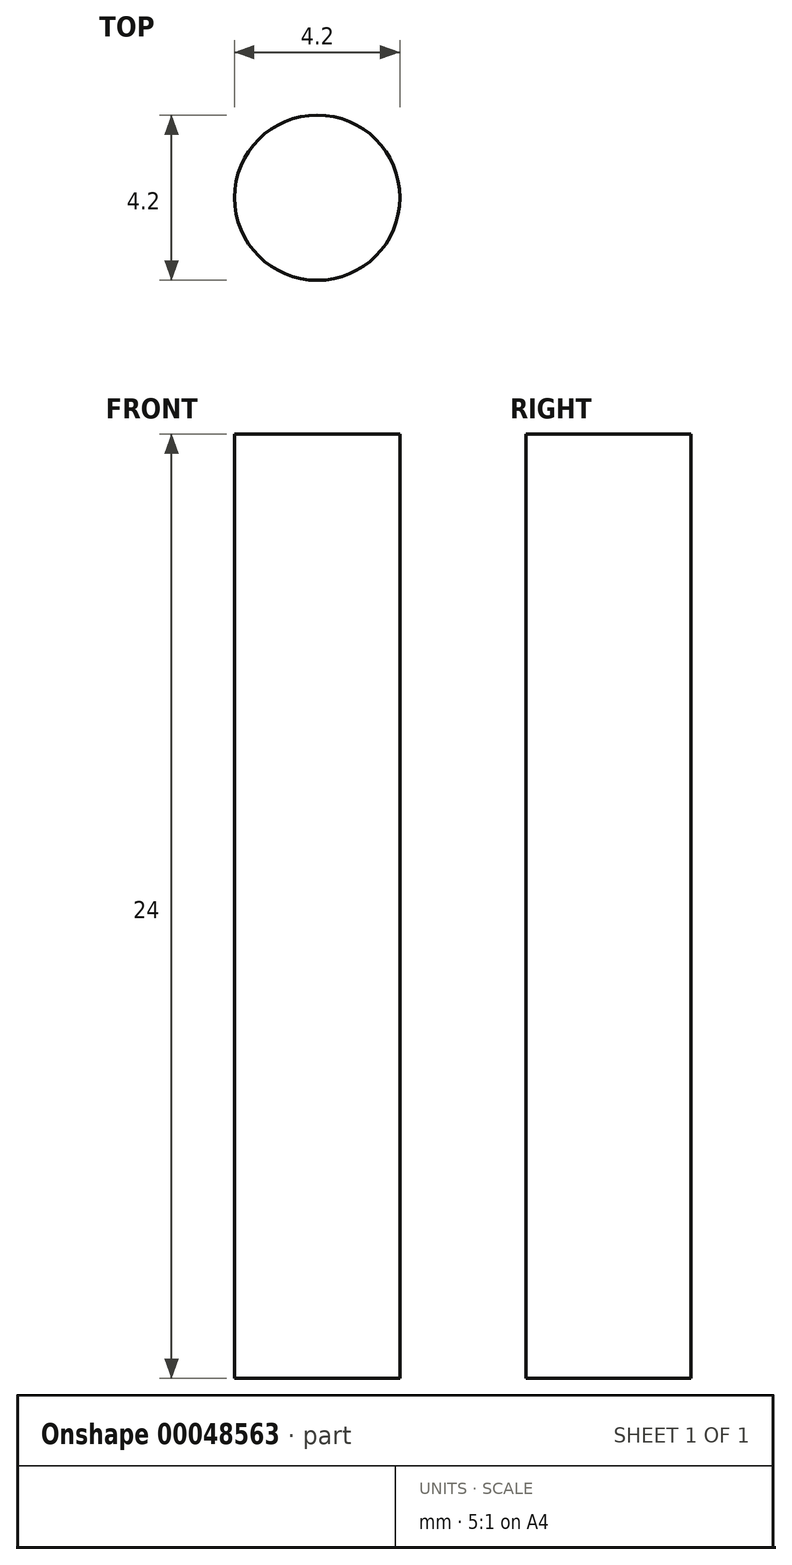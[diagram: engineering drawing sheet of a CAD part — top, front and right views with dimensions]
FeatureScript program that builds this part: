
annotation { "Feature Type Name" : "Feature", "Feature Type Description" : "" }
export const myFeature = defineFeature(function(context is Context, id is Id, definition is map)
    precondition{}
    {
        {
            var Q0;
            Q0=qCreatedBy(makeId("Top.planeOp"),FACE);
            var sketch = newSketch(context, id + "F0", { "sketchPlane" : qUnion([Q0])});
            skCircle(sketch, "E0", {"center": v(0, 0) * mm, "radius": 2.1 * mm});
            skSolve(sketch);
        }
        {
            var Q0;
            Q0=makeQuery(id+"F0.imprint","IMPRINT",FACE,{"disambiguationData":[TD([[makeQuery(id+"F0.imprint","IMPRINT",EDGE,{"derivedFrom":sQuery(id+"F0.wireOp",EDGE,"E0")}),1.0]])]});
            extrude(context, id + "F1", {"entities" : qUnion([Q0]), "depth" : 24 * mm});
        }
    });
